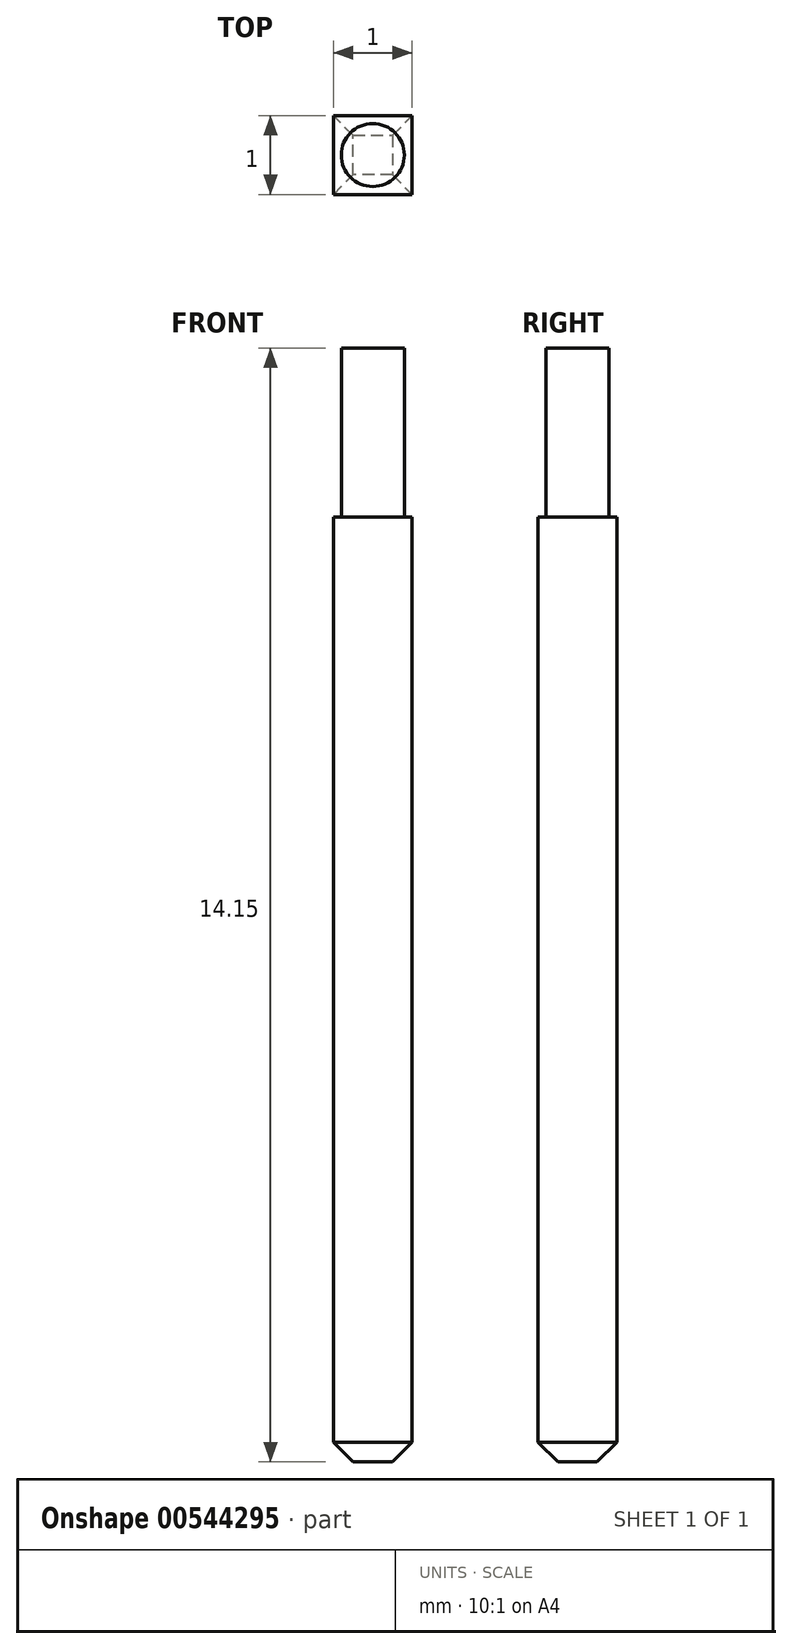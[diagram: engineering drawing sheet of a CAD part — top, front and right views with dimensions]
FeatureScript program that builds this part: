
annotation { "Feature Type Name" : "Feature", "Feature Type Description" : "" }
export const myFeature = defineFeature(function(context is Context, id is Id, definition is map)
    precondition{}
    {
        {
            var Q0;
            Q0=qCreatedBy(makeId("Top.planeOp"),FACE);
            var sketch = newSketch(context, id + "F0", { "sketchPlane" : qUnion([Q0])});
            skLineSegment(sketch, "E0.bottom", {"start": v(0, 0) * mm, "end": v(1, 0) * mm});
            skLineSegment(sketch, "E0.top", {"start": v(0, 1) * mm, "end": v(1, 1) * mm});
            skLineSegment(sketch, "E0.left", {"start": v(0, 0) * mm, "end": v(0, 1) * mm});
            skLineSegment(sketch, "E0.right", {"start": v(1, 0) * mm, "end": v(1, 1) * mm});
            skSolve(sketch);
        }
        {
            var Q0;
            Q0=qSketchRegion(id+"F0",true);
            extrude(context, id + "F1", {"entities" : qUnion([Q0]), "depth" : 12 * mm});
        }
        {
            var Q0;
            Q0=makeQuery(id+"F1.opExtrude","CAP_FACE",FACE,{"disambiguationData":[OSD([sQuery(id+"F0.wireOp",EDGE,"E0.bottom"),sQuery(id+"F0.wireOp",EDGE,"E0.top"),sQuery(id+"F0.wireOp",EDGE,"E0.left"),sQuery(id+"F0.wireOp",EDGE,"E0.right")])],"isStart":false});
            var sketch = newSketch(context, id + "F2", { "sketchPlane" : qUnion([Q0])});
            skCircle(sketch, "E1", {"center": v(0.5, 0.5) * mm, "radius": 0.4 * mm});
            skPoint(sketch, "E1.centerSnap0", {"position": v(1, 0.5) * mm});
            skSolve(sketch);
        }
        {
            var Q0;
            Q0=qSketchRegion(id+"F2",true);
            extrude(context, id + "F3", {"entities" : qUnion([Q0]), "operationType" : NewBodyOperationType.ADD, "depth" : 2.15 * mm});
        }
        {
            var Q0;
            Q0=makeQuery(id+"F1.opExtrude","CAP_EDGE",EDGE,{"disambiguationData":[OSD([sQuery(id+"F0.wireOp",EDGE,"E0.bottom")])],"isStart":true});
            var Q1;
            Q1=makeQuery(id+"F1.opExtrude","CAP_EDGE",EDGE,{"disambiguationData":[OSD([sQuery(id+"F0.wireOp",EDGE,"E0.left")])],"isStart":true});
            var Q2;
            Q2=makeQuery(id+"F1.opExtrude","CAP_EDGE",EDGE,{"disambiguationData":[OSD([sQuery(id+"F0.wireOp",EDGE,"E0.right")])],"isStart":true});
            var Q3;
            Q3=makeQuery(id+"F1.opExtrude","CAP_EDGE",EDGE,{"disambiguationData":[OSD([sQuery(id+"F0.wireOp",EDGE,"E0.top")])],"isStart":true});
            chamfer(context, id + "F4", {"entities" : qUnion([Q0, Q1, Q2, Q3]), "width" : 0.25 * mm, "tangentPropagation" : true});
        }
    });
